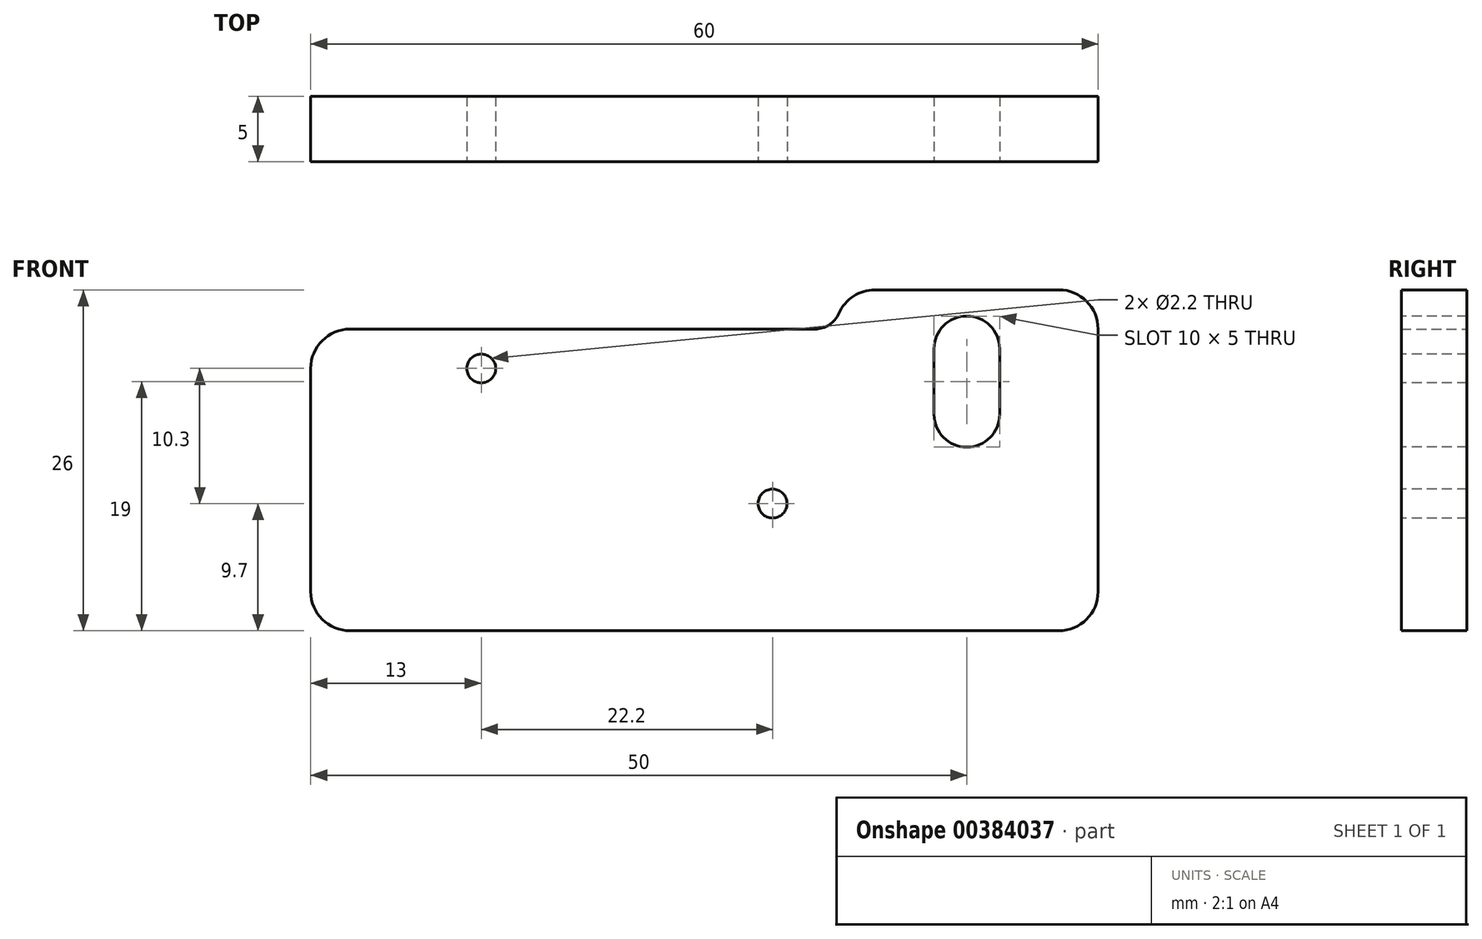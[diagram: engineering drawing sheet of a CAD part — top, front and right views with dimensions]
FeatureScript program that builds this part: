
annotation { "Feature Type Name" : "Feature", "Feature Type Description" : "" }
export const myFeature = defineFeature(function(context is Context, id is Id, definition is map)
    precondition{}
    {
        {
            var Q0;
            Q0=qCreatedBy(makeId("Front.planeOp"),FACE);
            var sketch = newSketch(context, id + "F0", { "sketchPlane" : qUnion([Q0])});
            skLineSegment(sketch, "E0", {"start": v(0, 0) * mm, "end": v(60, 0) * mm});
            skLineSegment(sketch, "E1", {"start": v(60, 0) * mm, "end": v(60, 26) * mm});
            skLineSegment(sketch, "E2", {"start": v(60, 26) * mm, "end": v(40, 26) * mm});
            skLineSegment(sketch, "E3", {"start": v(40, 26) * mm, "end": v(40, 23) * mm});
            skLineSegment(sketch, "E4", {"start": v(40, 23) * mm, "end": v(0, 23) * mm});
            skLineSegment(sketch, "E5", {"start": v(0, 23) * mm, "end": v(0, 0) * mm});
            skSolve(sketch);
        }
        {
            var Q0;
            Q0 = qSketchRegion(id + "F0", true);
            extrude(context, id + "F1", {"entities" : qUnion([Q0]), "depth" : 5 * mm});
        }
        {
            var Q0;
            Q0=makeQuery(id+"F1.opExtrude","CAP_FACE",FACE,{"disambiguationData":[OSD([sQuery(id+"F0.wireOp",EDGE,"E0"),sQuery(id+"F0.wireOp",EDGE,"E1"),sQuery(id+"F0.wireOp",EDGE,"E2"),sQuery(id+"F0.wireOp",EDGE,"E3"),sQuery(id+"F0.wireOp",EDGE,"E4"),sQuery(id+"F0.wireOp",EDGE,"E5")])],"isStart":false});
            var sketch = newSketch(context, id + "F2", { "sketchPlane" : qUnion([Q0])});
            skLineSegment(sketch, "E6", {"start": v(50, 21.5) * mm, "end": v(50, 16.5) * mm, "construction": true});
            skArc(sketch, "E7.0.startCap", {"start": v(47.5, 21.5) * mm, "mid": v(50, 24) * mm, "end": v(52.5, 21.5) * mm});
            skArc(sketch, "E7.0.endCap", {"start": v(52.5, 16.5) * mm, "mid": v(50, 14) * mm, "end": v(47.5, 16.5) * mm});
            skLineSegment(sketch, "E7.0.left", {"start": v(52.5, 21.5) * mm, "end": v(52.5, 16.5) * mm});
            skLineSegment(sketch, "E7.0.right", {"start": v(47.5, 21.5) * mm, "end": v(47.5, 16.5) * mm});
            skPoint(sketch, "E8", {"position": v(50, 19) * mm});
            skSolve(sketch);
        }
        {
            var Q0;
            Q0 = qSketchRegion(id + "F2", true);
            extrude(context, id + "F3", {"entities" : qUnion([Q0]), "operationType" : NewBodyOperationType.REMOVE, "endBound" : BoundingType.THROUGH_ALL, "oppositeDirection" : true, "depth" : 25 * mm});
        }
        {
            var Q0;
            Q0=makeQuery(id+"F1.opExtrude","CAP_FACE",FACE,{"disambiguationData":[OSD([sQuery(id+"F0.wireOp",EDGE,"E0"),sQuery(id+"F0.wireOp",EDGE,"E1"),sQuery(id+"F0.wireOp",EDGE,"E2"),sQuery(id+"F0.wireOp",EDGE,"E3"),sQuery(id+"F0.wireOp",EDGE,"E4"),sQuery(id+"F0.wireOp",EDGE,"E5")])],"isStart":false});
            var sketch = newSketch(context, id + "F4", { "sketchPlane" : qUnion([Q0])});
            skCircle(sketch, "E9", {"center": v(13, 20) * mm, "radius": 1.1 * mm});
            skCircle(sketch, "E10", {"center": v(35.2, 9.7) * mm, "radius": 1.1 * mm});
            skSolve(sketch);
        }
        {
            var Q0;
            Q0 = qSketchRegion(id + "F4", true);
            extrude(context, id + "F5", {"entities" : qUnion([Q0]), "operationType" : NewBodyOperationType.REMOVE, "endBound" : BoundingType.THROUGH_ALL, "oppositeDirection" : true, "depth" : 25 * mm});
        }
        {
            var Q0;
            Q0=makeQuery(id+"F1.opExtrude","SWEPT_EDGE",EDGE,{"disambiguationData":[OSD([sQuery(id+"F0.wireOp",EDGE,"E4"),sQuery(id+"F0.wireOp",EDGE,"E5")])]});
            var Q1;
            Q1=makeQuery(id+"F1.opExtrude","SWEPT_EDGE",EDGE,{"disambiguationData":[OSD([sQuery(id+"F0.wireOp",EDGE,"E1"),sQuery(id+"F0.wireOp",EDGE,"E2")])]});
            var Q2;
            Q2=makeQuery(id+"F1.opExtrude","SWEPT_EDGE",EDGE,{"disambiguationData":[OSD([sQuery(id+"F0.wireOp",EDGE,"E0"),sQuery(id+"F0.wireOp",EDGE,"E1")])]});
            var Q3;
            Q3=makeQuery(id+"F1.opExtrude","SWEPT_EDGE",EDGE,{"disambiguationData":[OSD([sQuery(id+"F0.wireOp",EDGE,"E0"),sQuery(id+"F0.wireOp",EDGE,"E5")])]});
            var Q4;
            Q4=makeQuery(id+"F1.opExtrude","SWEPT_EDGE",EDGE,{"disambiguationData":[OSD([sQuery(id+"F0.wireOp",EDGE,"E2"),sQuery(id+"F0.wireOp",EDGE,"E3")])]});
            fillet(context, id + "F6", {"entities" : qUnion([Q0, Q1, Q2, Q3, Q4]), "radius" : 3 * mm, "tangentPropagation" : true, "allowEdgeOverflow" : false});
        }
        {
            var Q0;
            Q0=makeQuery(id+"F6.opFillet","BLEND_EDGE",EDGE,{"blendedFrom":[makeQuery(id+"F1.opExtrude","SWEPT_EDGE",EDGE,{"disambiguationData":[OSD([sQuery(id+"F0.wireOp",EDGE,"E2"),sQuery(id+"F0.wireOp",EDGE,"E3")])]}),makeQuery(id+"F1.opExtrude","SWEPT_FACE",FACE,{"disambiguationData":[OSD([sQuery(id+"F0.wireOp",EDGE,"E4")])]})],"blendedInto":[makeQuery(id+"F1.opExtrude","SWEPT_FACE",FACE,{"disambiguationData":[OSD([sQuery(id+"F0.wireOp",EDGE,"E4")])]})]});
            fillet(context, id + "F7", {"entities" : qUnion([Q0]), "radius" : 2 * mm, "tangentPropagation" : true, "allowEdgeOverflow" : false});
        }
    });
